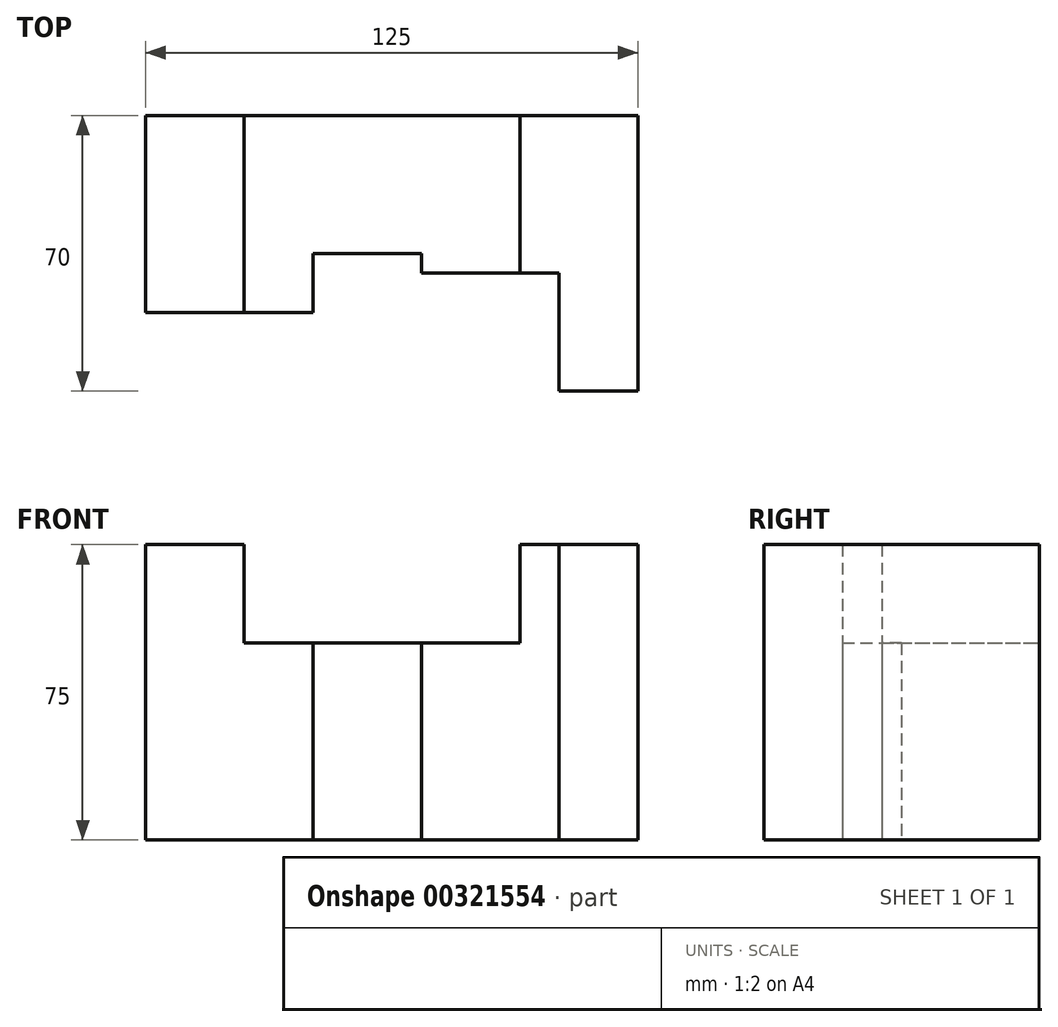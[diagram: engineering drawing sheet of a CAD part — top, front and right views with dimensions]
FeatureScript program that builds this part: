
annotation { "Feature Type Name" : "Feature", "Feature Type Description" : "" }
export const myFeature = defineFeature(function(context is Context, id is Id, definition is map)
    precondition{}
    {
        {
            var Q0;
            Q0=qCreatedBy(makeId("Top.planeOp"),FACE);
            var sketch = newSketch(context, id + "F0", { "sketchPlane" : qUnion([Q0])});
            skLineSegment(sketch, "E0.bottom", {"start": v(0, 0) * mm, "end": v(-125, 0) * mm});
            skLineSegment(sketch, "E0.top", {"start": v(0, -70) * mm, "end": v(-20, -70) * mm});
            skLineSegment(sketch, "E0.left", {"start": v(0, 0) * mm, "end": v(0, -70) * mm});
            skLineSegment(sketch, "E0.right", {"start": v(-125, 0) * mm, "end": v(-125, -50) * mm});
            skLineSegment(sketch, "E1", {"start": v(-20, -60) * mm, "end": v(-20, -70) * mm});
            skLineSegment(sketch, "E2", {"start": v(-125, -50) * mm, "end": v(-82.5, -50) * mm});
            skLineSegment(sketch, "E3", {"start": v(-82.5, -50) * mm, "end": v(-82.5, -35) * mm});
            skLineSegment(sketch, "E4", {"start": v(-82.5, -35) * mm, "end": v(-55, -35) * mm});
            skLineSegment(sketch, "E5", {"start": v(-55, -35) * mm, "end": v(-55, -40) * mm});
            skLineSegment(sketch, "E6", {"start": v(-55, -40) * mm, "end": v(-20, -40) * mm});
            skLineSegment(sketch, "E7", {"start": v(-20, -40) * mm, "end": v(-20, -70) * mm});
            skSolve(sketch);
        }
        {
            var Q0;
            Q0=makeQuery(id+"F0.imprint","IMPRINT",FACE,{"disambiguationData":[TD([[makeQuery(id+"F0.imprint","IMPRINT",EDGE,{"derivedFrom":sQuery(id+"F0.wireOp",EDGE,"E0.bottom")}),1.0]])]});
            extrude(context, id + "F1", {"entities" : qUnion([Q0]), "depth" : 50 * mm});
        }
        {
            var Q0;
            Q0=makeQuery(id+"F1.opExtrude","CAP_FACE",FACE,{"disambiguationData":[OSD([sQuery(id+"F0.wireOp",EDGE,"E0.bottom"),sQuery(id+"F0.wireOp",EDGE,"E0.top"),sQuery(id+"F0.wireOp",EDGE,"E0.left"),sQuery(id+"F0.wireOp",EDGE,"E0.right"),sQuery(id+"F0.wireOp",EDGE,"E2"),sQuery(id+"F0.wireOp",EDGE,"E3"),sQuery(id+"F0.wireOp",EDGE,"E4"),sQuery(id+"F0.wireOp",EDGE,"E5"),sQuery(id+"F0.wireOp",EDGE,"E6"),sQuery(id+"F0.wireOp",EDGE,"E7")])],"isStart":false});
            var sketch = newSketch(context, id + "F2", { "sketchPlane" : qUnion([Q0])});
            skLineSegment(sketch, "E8.bottom", {"start": v(-125, -50) * mm, "end": v(-100, -50) * mm});
            skLineSegment(sketch, "E8.top", {"start": v(-125, 0) * mm, "end": v(-100, 0) * mm});
            skLineSegment(sketch, "E8.left", {"start": v(-125, -50) * mm, "end": v(-125, 0) * mm});
            skLineSegment(sketch, "E8.right", {"start": v(-100, -50) * mm, "end": v(-100, 0) * mm});
            skSolve(sketch);
        }
        {
            var Q0;
            Q0=makeQuery(id+"F2.imprint","IMPRINT",FACE,{"disambiguationData":[TD([[makeQuery(id+"F2.imprint","IMPRINT",EDGE,{"derivedFrom":sQuery(id+"F2.wireOp",EDGE,"E8.bottom")}),1.0]])]});
            extrude(context, id + "F3", {"entities" : qUnion([Q0]), "operationType" : NewBodyOperationType.ADD, "depth" : 25 * mm});
        }
        {
            var Q0;
            Q0=makeQuery(id+"F1.opExtrude","CAP_FACE",FACE,{"disambiguationData":[OSD([sQuery(id+"F0.wireOp",EDGE,"E0.bottom"),sQuery(id+"F0.wireOp",EDGE,"E0.top"),sQuery(id+"F0.wireOp",EDGE,"E0.left"),sQuery(id+"F0.wireOp",EDGE,"E0.right"),sQuery(id+"F0.wireOp",EDGE,"E2"),sQuery(id+"F0.wireOp",EDGE,"E3"),sQuery(id+"F0.wireOp",EDGE,"E4"),sQuery(id+"F0.wireOp",EDGE,"E5"),sQuery(id+"F0.wireOp",EDGE,"E6"),sQuery(id+"F0.wireOp",EDGE,"E7")])],"isStart":false});
            var sketch = newSketch(context, id + "F4", { "sketchPlane" : qUnion([Q0])});
            skLineSegment(sketch, "E9", {"start": v(0, -70) * mm, "end": v(-20, -70) * mm});
            skLineSegment(sketch, "E10", {"start": v(-20, -70) * mm, "end": v(-20, -40) * mm});
            skLineSegment(sketch, "E11", {"start": v(-20, -40) * mm, "end": v(-30, -40) * mm});
            skLineSegment(sketch, "E12", {"start": v(-30, -40) * mm, "end": v(-30, 0) * mm});
            skLineSegment(sketch, "E13", {"start": v(-30, 0) * mm, "end": v(0, 0) * mm});
            skLineSegment(sketch, "E14", {"start": v(0, 0) * mm, "end": v(0, -70) * mm});
            skSolve(sketch);
        }
        {
            var Q0;
            Q0=makeQuery(id+"F4.imprint","IMPRINT",FACE,{"disambiguationData":[TD([[makeQuery(id+"F4.imprint","IMPRINT",EDGE,{"derivedFrom":sQuery(id+"F4.wireOp",EDGE,"E9")}),-1.0]])]});
            extrude(context, id + "F5", {"entities" : qUnion([Q0]), "operationType" : NewBodyOperationType.ADD, "depth" : 25 * mm});
        }
    });
